# Revit family: SonoMeter40_DN15-DN20_RFA
name_source: partatom
category: Pipe Accessories
revit_build: Autodesk Revit 2017 (Build: 20161205_1400(x64)
units: mm (PartAtom-declared; Revit-internal decimal feet)

## family parameters
Always vertical = Yes
Cut with Voids When Loaded = No
Part Type = Valve - Breaks Into
Round Connector Dimension = Use Diameter
Shared = No
Work Plane-Based = No

## types (9) — shared parameters
A = 45.00°
Body Material = Danfoss Brass
D = 15 mm  [stored 0.0492126 ft]
Description = Energy Meter
IfcExportAs = IfcValveType
IfcExportType = SonoMeter40
L1 = 122 mm
L6 = 8 mm  [stored 0.0262467 ft]
LOD 200 = No
LOD 350 = Yes
Manufacturer = Danfoss
Model = SonoMeter40
Operation Pressure = PN25
URL = https://store.danfoss.com

## per-type parameters (varying)
| type | A_H | Connection | D1 | D2 | H | H1 | H2 | Kvs | L | L2 | L3 | L4 | L5 | L7 | L_1 | Max Flow | Min Flow | Model Type | Nominal Flow | Weight |
| SonoMeter40_DN15_G3/4_Kvs2.27_110mm | 42 mm | G3/4B | 25 mm  [stored 0.082021 ft] | 26 mm | 65 mm  [stored 0.213255 ft] | 28 mm  [stored 0.0918635 ft] | 15 mm  [stored 0.0492126 ft] | 2.3 m³/h | 110 mm  [stored 0.360892 ft] | 59 mm | 59 mm | 12 mm  [stored 0.0393701 ft] | 86 mm  [stored 0.282152 ft] | 57 mm  [stored 0.187008 ft] | 8 mm  [stored 0.0262467 ft] | 1.2 m3/h | 0.006 m3/h | SonoMeter40_DN15_G3/4_Kvs2.27_110mm | 0.6 m3/h | 0.70 kg |
| SonoMeter40_DN15_G3/4_Kvs2.97_110mm | 42 mm | G3/4B | 25 mm  [stored 0.082021 ft] | 26 mm | 65 mm  [stored 0.213255 ft] | 28 mm  [stored 0.0918635 ft] | 15 mm  [stored 0.0492126 ft] | 3.0 m³/h | 110 mm  [stored 0.360892 ft] | 59 mm | 59 mm | 12 mm  [stored 0.0393701 ft] | 86 mm  [stored 0.282152 ft] | 57 mm  [stored 0.187008 ft] | 8 mm  [stored 0.0262467 ft] | 1.2 m3/h, 2.0 m3/h | 0.006 m3/h, 0.01 m3/h | SonoMeter40_DN15_G3/4_Kvs2.97_110mm | 0.6 m3/h, 1.0 m3/h | 0.70 kg |
| SonoMeter40_DN15_G3/4_Kvs3.63_110mm | 42 mm | G3/4B | 25 mm  [stored 0.082021 ft] | 26 mm | 65 mm  [stored 0.213255 ft] | 28 mm  [stored 0.0918635 ft] | 15 mm  [stored 0.0492126 ft] | 3.6 m³/h | 110 mm  [stored 0.360892 ft] | 59 mm | 59 mm | 12 mm  [stored 0.0393701 ft] | 86 mm  [stored 0.282152 ft] | 57 mm  [stored 0.187008 ft] | 8 mm  [stored 0.0262467 ft] | 3.0 m3/h | 0.015 m3/h | SonoMeter40_DN15_G3/4_Kvs3.63_110mm | 1.5 m3/h | 0.70 kg |
| SonoMeter40_DN15_G3/4_Kvs3.63_165mm | 42 mm | G3/4B | 25 mm  [stored 0.082021 ft] | 26 mm | 65 mm  [stored 0.213255 ft] | 28 mm  [stored 0.0918635 ft] | 15 mm  [stored 0.0492126 ft] | 3.6 m³/h | 165 mm | 87 mm | 83 mm | 14 mm  [stored 0.0459318 ft] | 138 mm | 77 mm | 17 mm  [stored 0.0557743 ft] | 3.0 m3/h | 0.015 m3/h | SonoMeter40_DN15_G3/4_Kvs3.63_110mm | 1.5 m3/h | 0.80 kg |
| SonoMeter40_DN20_G1_Kvs5.59_130mm | 41 mm | G1B | 30 mm  [stored 0.0984252 ft] | 33 mm | 65 mm  [stored 0.213255 ft] | 28 mm  [stored 0.0918635 ft] | 15 mm  [stored 0.0492126 ft] | 5.6 m³/h | 130 mm | 69 mm | 65 mm  [stored 0.213255 ft] | 14 mm  [stored 0.0459318 ft] | 102 mm | 77 mm | 6 mm  [stored 0.019685 ft] | 3.0 m3/h | 0.015 m3/h | SonoMeter40_DN20_G1_Kvs5.59_130mm | 1.5 m3/h | 0.80 kg |
| SonoMeter40_DN20_G1_Kvs6.23_190mm | 40 mm | G1B | 31 mm | 33 mm | 66 mm | 29 mm | 16 mm  [stored 0.0524934 ft] | 6.2 m³/h | 190 mm  [stored 0.62336 ft] | 95 mm | 95 mm | 14 mm  [stored 0.0459318 ft] | 159 mm | 130 mm | 11 mm  [stored 0.0360892 ft] | 1.2 m3/h, 2.0 m3/h | 0.006 m3/h, 0.01 m3/h | SonoMeter40_DN20_G1_Kvs6.23_190mm | 0.6 m3/h, 1.0 m3/h | 0.90 kg |
| SonoMeter40_DN20_G1_Kvs5.62_130mm | 41 mm | G1B | 30 mm  [stored 0.0984252 ft] | 33 mm | 65 mm  [stored 0.213255 ft] | 28 mm  [stored 0.0918635 ft] | 15 mm  [stored 0.0492126 ft] | 5.6 m³/h | 130 mm | 69 mm | 65 mm  [stored 0.213255 ft] | 14 mm  [stored 0.0459318 ft] | 102 mm | 77 mm | 6 mm  [stored 0.019685 ft] | 5.0 m3/h | 0.025 m3/h | SonoMeter40_DN20_G1_Kvs5.62_130mm | 2.5 m3/h | 0.80 kg |
| SonoMeter40_DN20_G1_Kvs8.15_190mm | 40 mm | G1B | 31 mm | 33 mm | 66 mm | 29 mm | 16 mm  [stored 0.0524934 ft] | 8.2 m³/h | 190 mm  [stored 0.62336 ft] | 95 mm | 95 mm | 14 mm  [stored 0.0459318 ft] | 159 mm | 130 mm | 11 mm  [stored 0.0360892 ft] | 5.0 m3/h | 0.025 m3/h | SonoMeter40_DN20_G1_Kvs8.15_190mm | 2.5 m3/h | 0.90 kg |
| SonoMeter40_DN20_G1_Kvs6.32_190mm | 40 mm | G1B | 31 mm | 33 mm | 66 mm | 29 mm | 16 mm  [stored 0.0524934 ft] | 6.3 m³/h | 190 mm  [stored 0.62336 ft] | 95 mm | 95 mm | 14 mm  [stored 0.0459318 ft] | 159 mm | 130 mm | 11 mm  [stored 0.0360892 ft] | 3.0 m3/h | 0.015 m3/h | SonoMeter40_DN20_G1_Kvs6.32_190mm | 1.5 m3/h | 0.90 kg |

note: [stored X ft] marks values corroborated as IEEE doubles in the binary element streams (Revit-internal decimal feet)

## geometry (parser evidence)
native form markers: Sweep x8
no freeform markers — native parametric forms only
